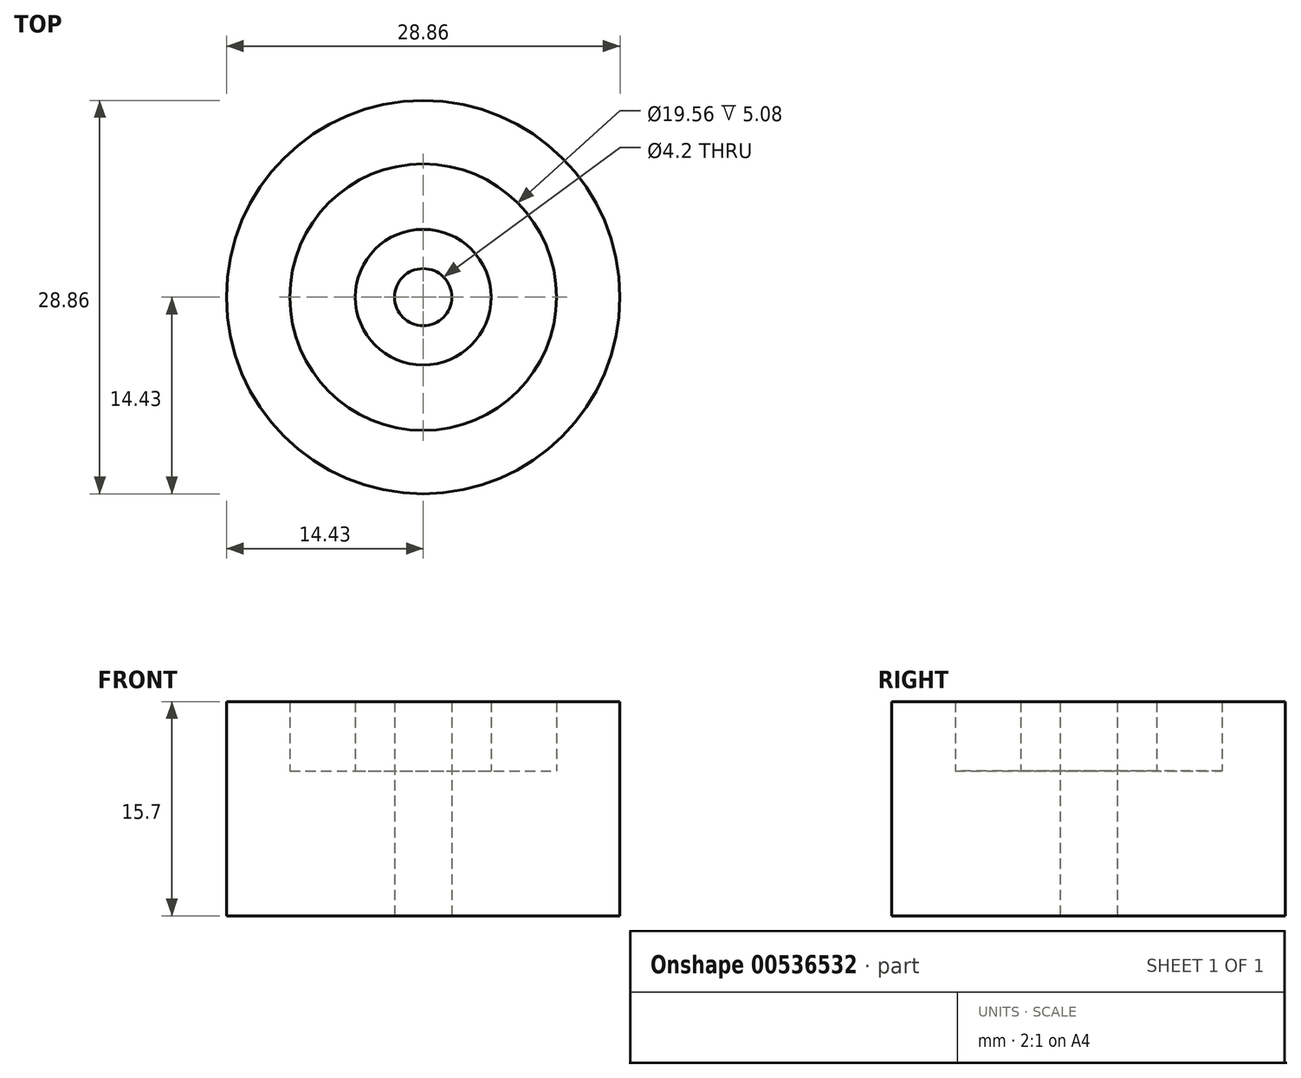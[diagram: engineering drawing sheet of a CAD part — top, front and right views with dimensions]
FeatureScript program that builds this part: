
annotation { "Feature Type Name" : "Feature", "Feature Type Description" : "" }
export const myFeature = defineFeature(function(context is Context, id is Id, definition is map)
    precondition{}
    {
        {
            var Q0;
            Q0=qCreatedBy(makeId("Front.planeOp"),FACE);
            var sketch = newSketch(context, id + "F0", { "sketchPlane" : qUnion([Q0])});
            skLineSegment(sketch, "E0", {"start": v(0, 0) * mm, "end": v(4.98, 0) * mm});
            skLineSegment(sketch, "E1", {"start": v(14.43, 0) * mm, "end": v(14.43, -15.7) * mm});
            skLineSegment(sketch, "E2", {"start": v(14.43, -15.7) * mm, "end": v(0, -15.7) * mm});
            skLineSegment(sketch, "E3", {"start": v(0, -15.7) * mm, "end": v(0, 0) * mm});
            skLineSegment(sketch, "E4", {"start": v(4.98, 0) * mm, "end": v(4.98, -5.08) * mm});
            skLineSegment(sketch, "E5", {"start": v(4.98, -5.08) * mm, "end": v(9.78, -5.08) * mm});
            skLineSegment(sketch, "E6", {"start": v(9.78, -5.08) * mm, "end": v(9.78, 0) * mm});
            skLineSegment(sketch, "E7", {"start": v(9.78, 0) * mm, "end": v(14.43, 0) * mm});
            skSolve(sketch);
        }
        {
            var Q0;
            Q0=qSketchRegion(id+"F0",true);
            var Q1;
            Q1=sQuery(id+"F0.wireOp",EDGE,"E3");
            revolve(context, id + "F1", {"entities" : qUnion([Q0]), "axis" : qUnion([Q1]), "revolveType" : RevolveType.FULL});
        }
        {
            var Q0;
            Q0=makeQuery(id+"F1.opRevolve","SWEPT_FACE",FACE,{"disambiguationData":[OSD([sQuery(id+"F0.wireOp",EDGE,"E0")])]});
            var sketch = newSketch(context, id + "F2", { "sketchPlane" : qUnion([Q0])});
            skPoint(sketch, "E8", {"position": v(0, 0) * mm});
            skSolve(sketch);
        }
        {
            var Q0;
            Q0=makeQuery(id+"F1.opRevolve","SWEPT_FACE",FACE,{"disambiguationData":[OSD([sQuery(id+"F0.wireOp",EDGE,"E2")])]});
            var sketch = newSketch(context, id + "F3", { "sketchPlane" : qUnion([Q0])});
            skLineSegment(sketch, "E9.bottom", {"start": v(-6.35, -6.35) * mm, "end": v(8.3, -6.35) * mm, "construction": true});
            skLineSegment(sketch, "E9.top", {"start": v(-6.35, 6.35) * mm, "end": v(8.3, 6.35) * mm, "construction": true});
            skLineSegment(sketch, "E9.left", {"start": v(-6.35, -6.35) * mm, "end": v(-6.35, 6.35) * mm, "construction": true});
            skLineSegment(sketch, "E9.right", {"start": v(8.3, -6.35) * mm, "end": v(8.3, 6.35) * mm, "construction": true});
            skLineSegment(sketch, "E10", {"start": v(-6.35, -6.35) * mm, "end": v(6.35, 6.35) * mm, "construction": true});
            skPoint(sketch, "E11", {"position": v(0, 0) * mm});
            skCircle(sketch, "E12", {"center": v(0, 0) * mm, "radius": 3.18 * mm, "construction": true});
            skSolve(sketch);
        }
        {
            var Q0;
            Q0=sQuery(id+"F3.wireOp",VERTEX,"E12.center");
            var Q1;
            Q1=makeQuery(id+"F1.opRevolve","SWEPT_BODY",BODY,{"disambiguationData":[OSD([sQuery(id+"F0.wireOp",EDGE,"E0"),sQuery(id+"F0.wireOp",EDGE,"E1"),sQuery(id+"F0.wireOp",EDGE,"uxOOcbma-rM4K-7eKG-5Tp7-zW7kDo2e6Tqz"),sQuery(id+"F0.wireOp",EDGE,"NVDGhDdD-NORQ-odFN-u7FE-xEci0S9tA2uR"),sQuery(id+"F0.wireOp",EDGE,"40iU4O4p-ozLo-chVG-qLtP-0FngMtXhOWi2"),sQuery(id+"F0.wireOp",EDGE,"CslwQrNs-j4zt-ha6i-uIB6-hjxAhkhzMRnj"),sQuery(id+"F0.wireOp",EDGE,"E2"),sQuery(id+"F0.wireOp",EDGE,"E3")])]});
            hole(context, id + "F4", {"style" : HoleStyle.SIMPLE, "endStyle" : HoleEndStyle.BLIND, "standardTappedOrClearance" : lookupTablePath({ "standard" : "ISO", "engagement" : "75%", "pitch" : "0.8 mm", "size" : "M5", "type" : "Tapped" }), "standardBlindInLast" : lookupTablePath({ "standard" : "ISO", "engagement" : "75%", "pitch" : "0.8 mm", "size" : "M5", "type" : "Tapped" }), "holeDiameter" : 4.2 * mm, "showTappedDepth" : true, "holeDepth" : 27.8 * mm, "tappedDepth" : 25.4 * mm, "tapClearance" : 3, "startFromSketch" : true, "locations" : qUnion([Q0]), "scope" : qUnion([Q1]), "majorDiameter" : 5 * mm});
        }
        {
            var Q0;
            Q0=sQuery(id+"F2.wireOp",VERTEX,"E8");
            var Q1;
            Q1=makeQuery(id+"F1.opRevolve","SWEPT_BODY",BODY,{"disambiguationData":[OSD([sQuery(id+"F0.wireOp",EDGE,"E0"),sQuery(id+"F0.wireOp",EDGE,"E1"),sQuery(id+"F0.wireOp",EDGE,"E2"),sQuery(id+"F0.wireOp",EDGE,"E3")])]});
            hole(context, id + "F5", {"style" : HoleStyle.SIMPLE, "endStyle" : HoleEndStyle.BLIND, "standardTappedOrClearance" : lookupTablePath({ "standard" : "ANSI", "engagement" : "75%", "pitch" : "32 tpi", "size" : "#8", "type" : "Tapped" }), "standardBlindInLast" : lookupTablePath({ "standard" : "ANSI", "engagement" : "75%", "pitch" : "32 tpi", "size" : "#8", "type" : "Tapped" }), "holeDiameter" : 3.45 * mm, "majorDiameter" : 4.17 * mm, "showTappedDepth" : true, "holeDepth" : 10.32 * mm, "tappedDepth" : 9.52 * mm, "tapClearance" : 1, "startFromSketch" : true, "locations" : qUnion([Q0]), "scope" : qUnion([Q1])});
        }
    });
